# Revit family: Wicslide_65_Glass24_3_leaf_2_track_dependent
name_source: partatom
category: Doors
revit_build: Autodesk Revit Architecture 2014 (Build: 20130308_1515(x64)
units: mm (PartAtom-declared; Revit-internal decimal feet)

## types (1)
- Wicslide_65_Glass24_3_leaf_2_track_dependent
    Acoustic = RA,tr = 35 dB
    Air Permeability = Class 4
    Analytic Construction = <None>
    Bottom Offset = 53 mm
    Corrosion Resistance of the Fittings = Class 5
    Date of publishing = 3/14/2015
    Description = With  its  various  designs  of  outer  and  opening  frames, multiple  leaf  combinations  (from  2  to  6  leaves)  and  its  comprehensive range of dual colour solutions, the Wicslide 65 brings greater freedom to building design. Designed  to  meet  market  demands,  Wicslide  65  sliding doors are perfectly suited for disabled access.
    Design country = Germany
    Door 1 connect = 791 mm
    Door Offset = 60 mm  [stored 0.19685 ft]
    EN1627 Burglar Resistance = RC1N, RC2N, RC2, RC3, SBD
    Edition number = 1
    Frame 1041226 = Yes
    Frame 1041231 = No
    Frame Bottom 1041226 = Yes
    Frame Bottom 1041231 = No
    Frame Bottom 1041232 = No
    Frame Depth = 65 mm  [stored 0.213255 ft]
    Frame Material = WICONA - Aluminium - RAL7016 - Anthracite Grey - Matt
    Frame Width = 67 mm
    Frame Width 2 = 48 mm
    Frame Width 3 = 33 mm
    Frame all = 1823 mm
    Function = Interior
    Glass Material = WICONA -  Glass
    Glass Width = 608 mm  [stored 1.99475 ft]
    Handle Material = Aluminium
    Height = 2100 mm
    Keynote = L10/330
    Leaf 2 Width = 681 mm
    Leaf 3 Width = 720 mm
    Leaf Connect = 6 mm  [stored 0.019685 ft]
    Leaf Height All = 2000 mm  [stored 6.56168 ft]
    Leaf Material = WICONA - Aluminium - RAL7016 - Anthracite Grey - Matt
    Leaf Width = 681 mm
    Load Bearing Capacity of Safety Devices = Fulfilled
    Manufacturer = Wicona
    Manufacturer country = Germany
    Manufacturer name = Wicona
    Maximum Sash Weight = 160kg as standard design, heavier weights can easily be customised
    Mechanical Strength = Class 4
    Model = Wicslide 65
    Nominal height = 210000
    Nominal width = 220000
    Operating Forces = Class 1
    Operation = IFC_DOORSLIDING
IFC_DOORSLIDING
    Product Guid = 74bd8be9-202c-4542-9c4e-775a99e34c85
    Product SKU = WICSLIDE_65_W
    Product data url = http://bimobject.com
    QR code = http://bimobject.com
    Quality Assurance = Certified according to ISO 9001:2008
    Repeated Opening/Closing = Class 3 (20,000 Cycles)
    Sash 1041260 = No
    Sash 1041261 = No
    Sash 1041262 = No
    Sash 1041263 = Yes
    Sash meeting 3041240 = No
    Sash meeting 3041241 = No
    Sash meeting 3041242 = Yes
    Thermal (2-leaf frame) = Uw < 1.5 W/m².K (with Ug = 1.0)
    URL = http://www.wicona.com
    Uniclass2 = Ss-25-30-95-28
    Wall Closure = By host
    Watertightness = E900
    Weight Net (Kg) = 0
    Width = 2200 mm

note: [stored X ft] marks values corroborated as IEEE doubles in the binary element streams (Revit-internal decimal feet)

## geometry (parser evidence)
native form markers: Blend x4, Sweep x42
no freeform markers — native parametric forms only
